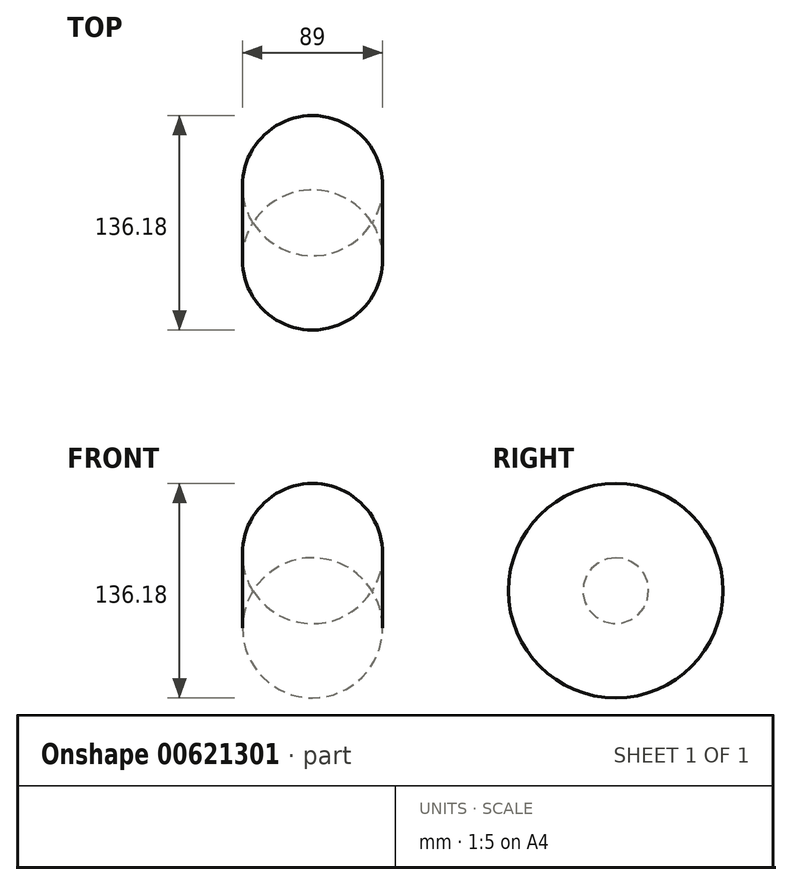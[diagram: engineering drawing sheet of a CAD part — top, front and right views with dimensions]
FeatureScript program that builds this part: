
annotation { "Feature Type Name" : "Feature", "Feature Type Description" : "" }
export const myFeature = defineFeature(function(context is Context, id is Id, definition is map)
    precondition{}
    {
        {
            var Q0;
            Q0=qCreatedBy(makeId("Front.planeOp"),FACE);
            var sketch = newSketch(context, id + "F0", { "sketchPlane" : qUnion([Q0])});
            skLineSegment(sketch, "E0", {"start": v(0, 0) * mm, "end": v(-75.46, 0) * mm});
            skArc(sketch, "E1", {"start": v(0, 0) * mm, "mid": v(-37.73, 20.9) * mm, "end": v(-75.46, 0) * mm});
            skSolve(sketch);
        }
        {
            var Q0;
            Q0=makeQuery(id+"F0.imprint","IMPRINT",FACE,{"disambiguationData":[TD([[makeQuery(id+"F0.imprint","IMPRINT",EDGE,{"derivedFrom":sQuery(id+"F0.wireOp",EDGE,"E0")}),-1.0]])]});
            var Q1;
            Q1=sQuery(id+"F0.wireOp",EDGE,"E0");
            revolve(context, id + "F1", {"entities" : qUnion([Q0]), "axis" : qUnion([Q1]), "revolveType" : RevolveType.FULL});
        }
    });
